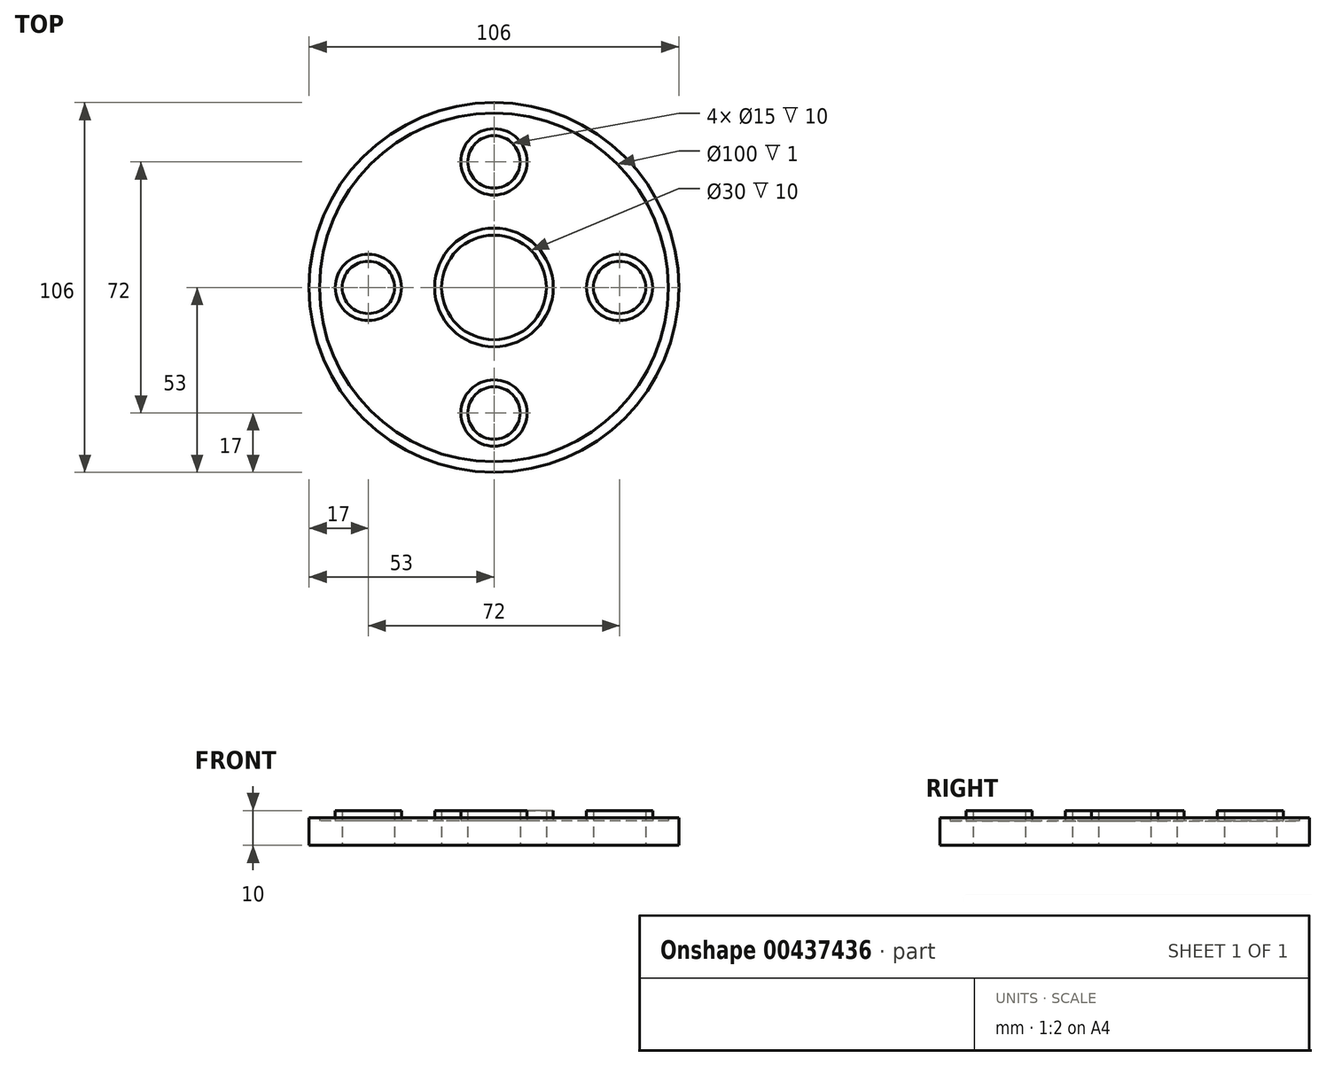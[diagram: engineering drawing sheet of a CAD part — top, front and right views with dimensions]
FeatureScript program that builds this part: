
annotation { "Feature Type Name" : "Feature", "Feature Type Description" : "" }
export const myFeature = defineFeature(function(context is Context, id is Id, definition is map)
    precondition{}
    {
        {
            var Q0;
            Q0=qCreatedBy(makeId("Top.planeOp"),FACE);
            var sketch = newSketch(context, id + "F0", { "sketchPlane" : qUnion([Q0])});
            skCircle(sketch, "E0", {"center": v(0, 0) * mm, "radius": 53 * mm});
            skCircle(sketch, "E1", {"center": v(0, 0) * mm, "radius": 50 * mm});
            skCircle(sketch, "E2", {"center": v(0, 36) * mm, "radius": 9.5 * mm});
            skCircle(sketch, "E3", {"center": v(0, 36) * mm, "radius": 7.5 * mm});
            skCircle(sketch, "E4", {"center": v(36, 0) * mm, "radius": 9.5 * mm});
            skCircle(sketch, "E5", {"center": v(36, 0) * mm, "radius": 7.5 * mm});
            skCircle(sketch, "E6", {"center": v(-36, 0) * mm, "radius": 9.5 * mm});
            skCircle(sketch, "E7", {"center": v(-36, 0) * mm, "radius": 7.5 * mm});
            skCircle(sketch, "E8", {"center": v(0, -36) * mm, "radius": 9.5 * mm});
            skCircle(sketch, "E9", {"center": v(0, -36) * mm, "radius": 7.5 * mm});
            skCircle(sketch, "E10", {"center": v(0, 0) * mm, "radius": 15 * mm});
            skCircle(sketch, "E11", {"center": v(0, 0) * mm, "radius": 17 * mm});
            skSolve(sketch);
        }
        {
            var Q0;
            Q0=makeQuery(id+"F0.imprint","IMPRINT",FACE,{"disambiguationData":[TD([[makeQuery(id+"F0.imprint","IMPRINT",EDGE,{"derivedFrom":sQuery(id+"F0.wireOp",EDGE,"E1")}),1.0]])]});
            extrude(context, id + "F1", {"entities" : qUnion([Q0]), "depth" : 7 * mm});
        }
        {
            var Q0;
            Q0=makeQuery(id+"F0.imprint","IMPRINT",FACE,{"disambiguationData":[TD([[makeQuery(id+"F0.imprint","IMPRINT",EDGE,{"derivedFrom":sQuery(id+"F0.wireOp",EDGE,"E0")}),1.0]])]});
            extrude(context, id + "F2", {"entities" : qUnion([Q0]), "operationType" : NewBodyOperationType.ADD, "depth" : 8 * mm});
        }
        {
            var Q0;
            Q0=makeQuery(id+"F0.imprint","IMPRINT",FACE,{"disambiguationData":[TD([[makeQuery(id+"F0.imprint","IMPRINT",EDGE,{"derivedFrom":sQuery(id+"F0.wireOp",EDGE,"E2")}),1.0]])]});
            var Q1;
            Q1=makeQuery(id+"F0.imprint","IMPRINT",FACE,{"disambiguationData":[TD([[makeQuery(id+"F0.imprint","IMPRINT",EDGE,{"derivedFrom":sQuery(id+"F0.wireOp",EDGE,"E6")}),1.0]])]});
            var Q2;
            Q2=makeQuery(id+"F0.imprint","IMPRINT",FACE,{"disambiguationData":[TD([[makeQuery(id+"F0.imprint","IMPRINT",EDGE,{"derivedFrom":sQuery(id+"F0.wireOp",EDGE,"E4")}),1.0]])]});
            var Q3;
            Q3=makeQuery(id+"F0.imprint","IMPRINT",FACE,{"disambiguationData":[TD([[makeQuery(id+"F0.imprint","IMPRINT",EDGE,{"derivedFrom":sQuery(id+"F0.wireOp",EDGE,"E8")}),1.0]])]});
            var Q4;
            Q4=makeQuery(id+"F0.imprint","IMPRINT",FACE,{"disambiguationData":[TD([[makeQuery(id+"F0.imprint","IMPRINT",EDGE,{"derivedFrom":sQuery(id+"F0.wireOp",EDGE,"E10")}),-1.0]])]});
            extrude(context, id + "F3", {"entities" : qUnion([Q0, Q1, Q2, Q3, Q4]), "operationType" : NewBodyOperationType.ADD, "depth" : 10 * mm});
        }
    });
